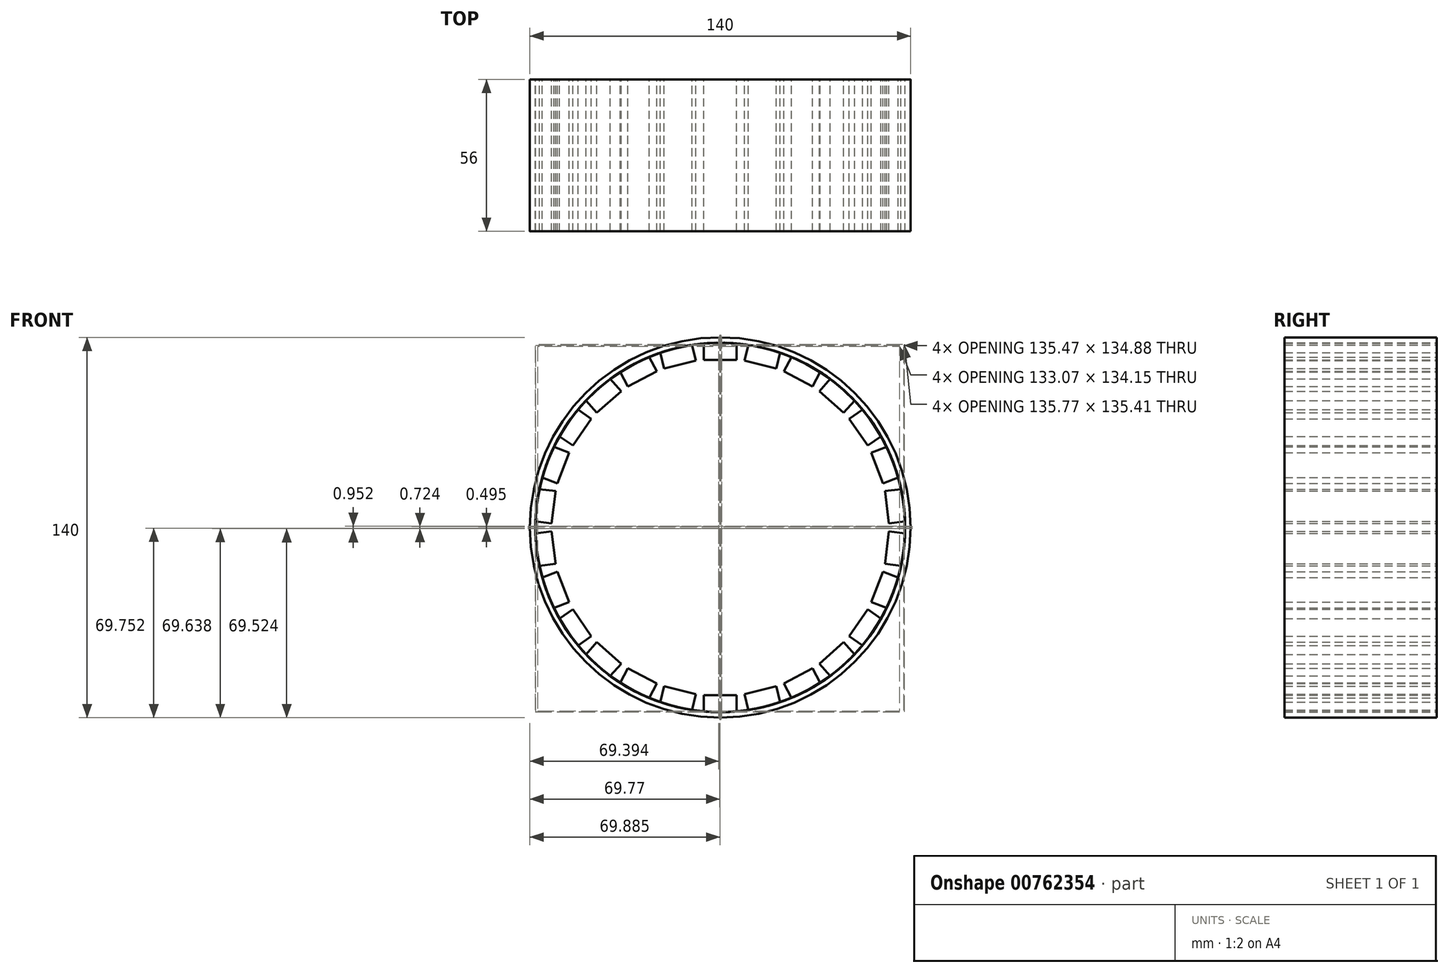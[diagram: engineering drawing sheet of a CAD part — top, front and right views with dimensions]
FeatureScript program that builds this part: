
annotation { "Feature Type Name" : "Feature", "Feature Type Description" : "" }
export const myFeature = defineFeature(function(context is Context, id is Id, definition is map)
    precondition{}
    {
        {
            var Q0;
            Q0=qCreatedBy(makeId("Front.planeOp"),FACE);
            var sketch = newSketch(context, id + "F0", { "sketchPlane" : qUnion([Q0])});
            skArc(sketch, "E0", {"start": v(-6, 67.73) * mm, "mid": v(0, -68) * mm, "end": v(6, 67.73) * mm});
            skLineSegment(sketch, "E1", {"start": v(6, 61.73) * mm, "end": v(6, 67.73) * mm});
            skCircle(sketch, "E2", {"center": v(0, 0) * mm, "radius": 70 * mm});
            skLineSegment(sketch, "E3", {"start": v(-6, 67.73) * mm, "end": v(-6, 61.73) * mm});
            skLineSegment(sketch, "E4", {"start": v(-6, 61.73) * mm, "end": v(6, 61.73) * mm});
            skSolve(sketch);
        }
        {
            var Q0;
            Q0=makeQuery(id+"F0.imprint","IMPRINT",FACE,{"disambiguationData":[TD([[makeQuery(id+"F0.imprint","IMPRINT",EDGE,{"derivedFrom":sQuery(id+"F0.wireOp",EDGE,"E0")}),-1.0]])]});
            extrude(context, id + "F1", {"entities" : qUnion([Q0]), "depth" : 56 * mm, "offsetDistance" : 25 * mm});
        }
        {
            var Q0;
            Q0=makeQuery(id+"F1.opExtrude","SWEPT_BODY",BODY,{"disambiguationData":[OSD([sQuery(id+"F0.wireOp",EDGE,"E0"),sQuery(id+"F0.wireOp",EDGE,"E1"),sQuery(id+"F0.wireOp",EDGE,"E2"),sQuery(id+"F0.wireOp",EDGE,"E3"),sQuery(id+"F0.wireOp",EDGE,"E4")])]});
            var Q1;
            Q1=makeQuery(id+"F1.opExtrude","SWEPT_FACE",FACE,{"disambiguationData":[OSD([sQuery(id+"F0.wireOp",EDGE,"E0")])]});
            circularPattern(context, id + "F2", {"entities" : qUnion([Q0]), "axis" : qUnion([Q1]), "angle" : 360 * degree, "instanceCount" : 26, "equalSpace" : true});
        }
    });
